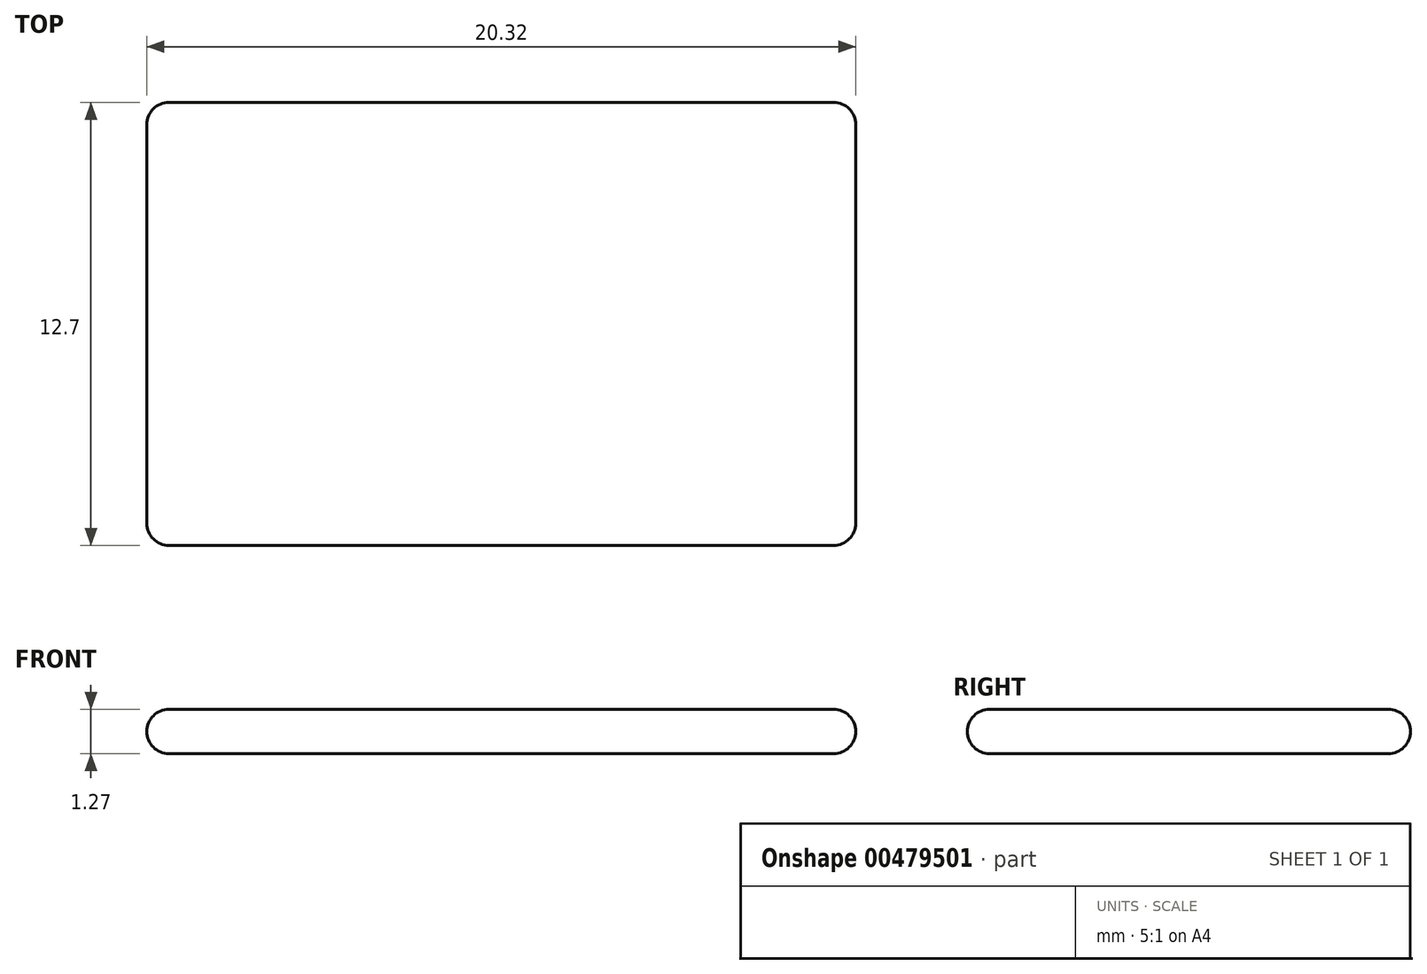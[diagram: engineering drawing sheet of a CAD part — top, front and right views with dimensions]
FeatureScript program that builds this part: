
annotation { "Feature Type Name" : "Feature", "Feature Type Description" : "" }
export const myFeature = defineFeature(function(context is Context, id is Id, definition is map)
    precondition{}
    {
        {
            var Q0;
            Q0=qCreatedBy(makeId("Top.planeOp"),FACE);
            var sketch = newSketch(context, id + "F0", { "sketchPlane" : qUnion([Q0])});
            skLineSegment(sketch, "E0", {"start": v(0, 0) * mm, "end": v(0, 12.7) * mm});
            skLineSegment(sketch, "E1", {"start": v(0, 12.7) * mm, "end": v(-20.32, 12.7) * mm});
            skLineSegment(sketch, "E2", {"start": v(-20.32, 12.7) * mm, "end": v(-20.32, 0) * mm});
            skLineSegment(sketch, "E3", {"start": v(-20.32, 0) * mm, "end": v(0, 0) * mm});
            skSolve(sketch);
        }
        {
            var Q0;
            Q0=makeQuery(id+"F0.imprint","IMPRINT",FACE,{"disambiguationData":[TD([[makeQuery(id+"F0.imprint","IMPRINT",EDGE,{"derivedFrom":sQuery(id+"F0.wireOp",EDGE,"E0")}),1.0]])]});
            extrude(context, id + "F1", {"entities" : qUnion([Q0]), "depth" : 1.27 * mm});
        }
        {
            var Q0;
            Q0=makeQuery(id+"F1.opExtrude","CAP_EDGE",EDGE,{"disambiguationData":[OSD([sQuery(id+"F0.wireOp",EDGE,"E0")])],"isStart":false});
            var Q1;
            Q1=makeQuery(id+"F1.opExtrude","CAP_EDGE",EDGE,{"disambiguationData":[OSD([sQuery(id+"F0.wireOp",EDGE,"E0")])],"isStart":true});
            fillet(context, id + "F2", {"entities" : qUnion([Q0, Q1]), "radius" : 0.64 * mm, "tangentPropagation" : true, "allowEdgeOverflow" : false});
        }
        {
            var Q0;
            Q0=makeQuery(id+"F1.opExtrude","CAP_EDGE",EDGE,{"disambiguationData":[OSD([sQuery(id+"F0.wireOp",EDGE,"E2")])],"isStart":false});
            fillet(context, id + "F3", {"entities" : qUnion([Q0]), "radius" : 0.64 * mm, "tangentPropagation" : true, "allowEdgeOverflow" : false});
        }
        {
            var Q0;
            Q0=makeQuery(id+"F1.opExtrude","CAP_EDGE",EDGE,{"disambiguationData":[OSD([sQuery(id+"F0.wireOp",EDGE,"E2")])],"isStart":true});
            fillet(context, id + "F4", {"entities" : qUnion([Q0]), "radius" : 0.64 * mm, "tangentPropagation" : true, "allowEdgeOverflow" : false});
        }
        {
            var Q0;
            Q0=makeQuery(id+"F1.opExtrude","CAP_EDGE",EDGE,{"disambiguationData":[OSD([sQuery(id+"F0.wireOp",EDGE,"E1")])],"isStart":false});
            fillet(context, id + "F5", {"entities" : qUnion([Q0]), "radius" : 0.64 * mm, "tangentPropagation" : true, "allowEdgeOverflow" : false});
        }
        {
            var Q0;
            Q0=makeQuery(id+"F1.opExtrude","CAP_EDGE",EDGE,{"disambiguationData":[OSD([sQuery(id+"F0.wireOp",EDGE,"E3")])],"isStart":false});
            fillet(context, id + "F6", {"entities" : qUnion([Q0]), "radius" : 0.64 * mm, "tangentPropagation" : true, "allowEdgeOverflow" : false});
        }
        {
            var Q0;
            Q0=qCreatedBy(makeId("Top.planeOp"),FACE);
            var sketch = newSketch(context, id + "F7", { "sketchPlane" : qUnion([Q0])});
            skLineSegment(sketch, "E4.bottom", {"start": v(-19, 11.41) * mm, "end": v(-1.25, 11.41) * mm});
            skLineSegment(sketch, "E4.top", {"start": v(-19, 1.34) * mm, "end": v(-1.25, 1.34) * mm});
            skLineSegment(sketch, "E4.left", {"start": v(-19, 11.41) * mm, "end": v(-19, 1.34) * mm});
            skLineSegment(sketch, "E4.right", {"start": v(-1.25, 11.41) * mm, "end": v(-1.25, 1.34) * mm});
            skSolve(sketch);
        }
        {
            var Q0;
            Q0 = qSketchRegion(id + "F7", true);
            extrude(context, id + "F8", {"entities" : qUnion([Q0]), "operationType" : NewBodyOperationType.ADD, "depth" : 1.27 * mm});
        }
    });
